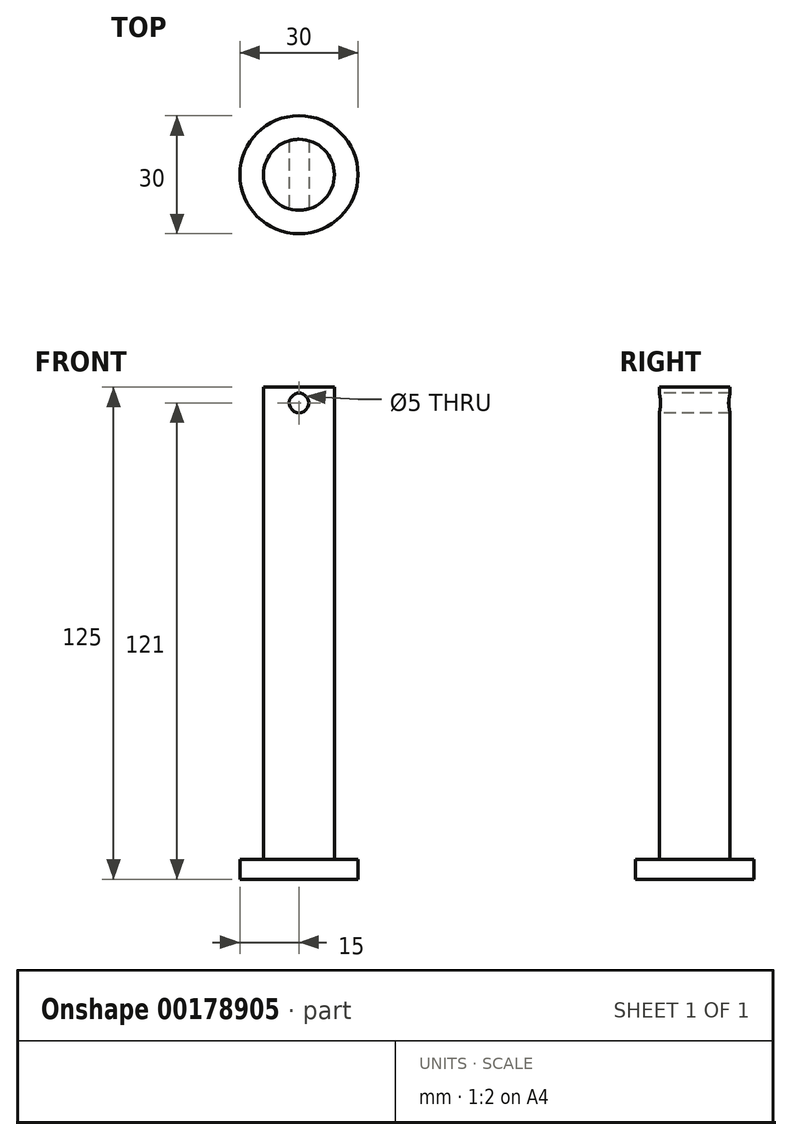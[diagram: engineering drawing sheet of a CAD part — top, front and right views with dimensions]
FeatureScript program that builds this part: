
annotation { "Feature Type Name" : "Feature", "Feature Type Description" : "" }
export const myFeature = defineFeature(function(context is Context, id is Id, definition is map)
    precondition{}
    {
        {
            var Q0;
            Q0=qCreatedBy(makeId("Top.planeOp"),FACE);
            var sketch = newSketch(context, id + "F0", { "sketchPlane" : qUnion([Q0])});
            skCircle(sketch, "E0", {"center": v(0, 0) * mm, "radius": 9 * mm});
            skSolve(sketch);
        }
        {
            var Q0;
            Q0=makeQuery(id+"F0.imprint","IMPRINT",FACE,{"disambiguationData":[TD([[makeQuery(id+"F0.imprint","IMPRINT",EDGE,{"derivedFrom":sQuery(id+"F0.wireOp",EDGE,"E0")}),1.0]])]});
            extrude(context, id + "F1", {"entities" : qUnion([Q0]), "depth" : 125 * mm});
        }
        {
            var Q0;
            Q0=qCreatedBy(makeId("Top.planeOp"),FACE);
            var sketch = newSketch(context, id + "F2", { "sketchPlane" : qUnion([Q0])});
            skCircle(sketch, "E1", {"center": v(0, 0) * mm, "radius": 15 * mm});
            skSolve(sketch);
        }
        {
            var Q0;
            Q0=makeQuery(id+"F2.imprint","IMPRINT",FACE,{"disambiguationData":[TD([[makeQuery(id+"F2.imprint","IMPRINT",EDGE,{"derivedFrom":sQuery(id+"F2.wireOp",EDGE,"E1")}),1.0]])]});
            extrude(context, id + "F3", {"entities" : qUnion([Q0]), "operationType" : NewBodyOperationType.ADD, "depth" : 5 * mm});
        }
        {
            var Q0;
            Q0=qCreatedBy(makeId("Front.planeOp"),FACE);
            var sketch = newSketch(context, id + "F4", { "sketchPlane" : qUnion([Q0])});
            skCircle(sketch, "E2", {"center": v(0, 121) * mm, "radius": 2.5 * mm});
            skSolve(sketch);
        }
        {
            var Q0;
            Q0=makeQuery(id+"F4.imprint","IMPRINT",FACE,{"disambiguationData":[TD([[makeQuery(id+"F4.imprint","IMPRINT",EDGE,{"derivedFrom":sQuery(id+"F4.wireOp",EDGE,"E2")}),1.0]])]});
            extrude(context, id + "F5", {"entities" : qUnion([Q0]), "operationType" : NewBodyOperationType.REMOVE, "endBound" : BoundingType.SYMMETRIC, "oppositeDirection" : true, "depth" : 25 * mm});
        }
    });
